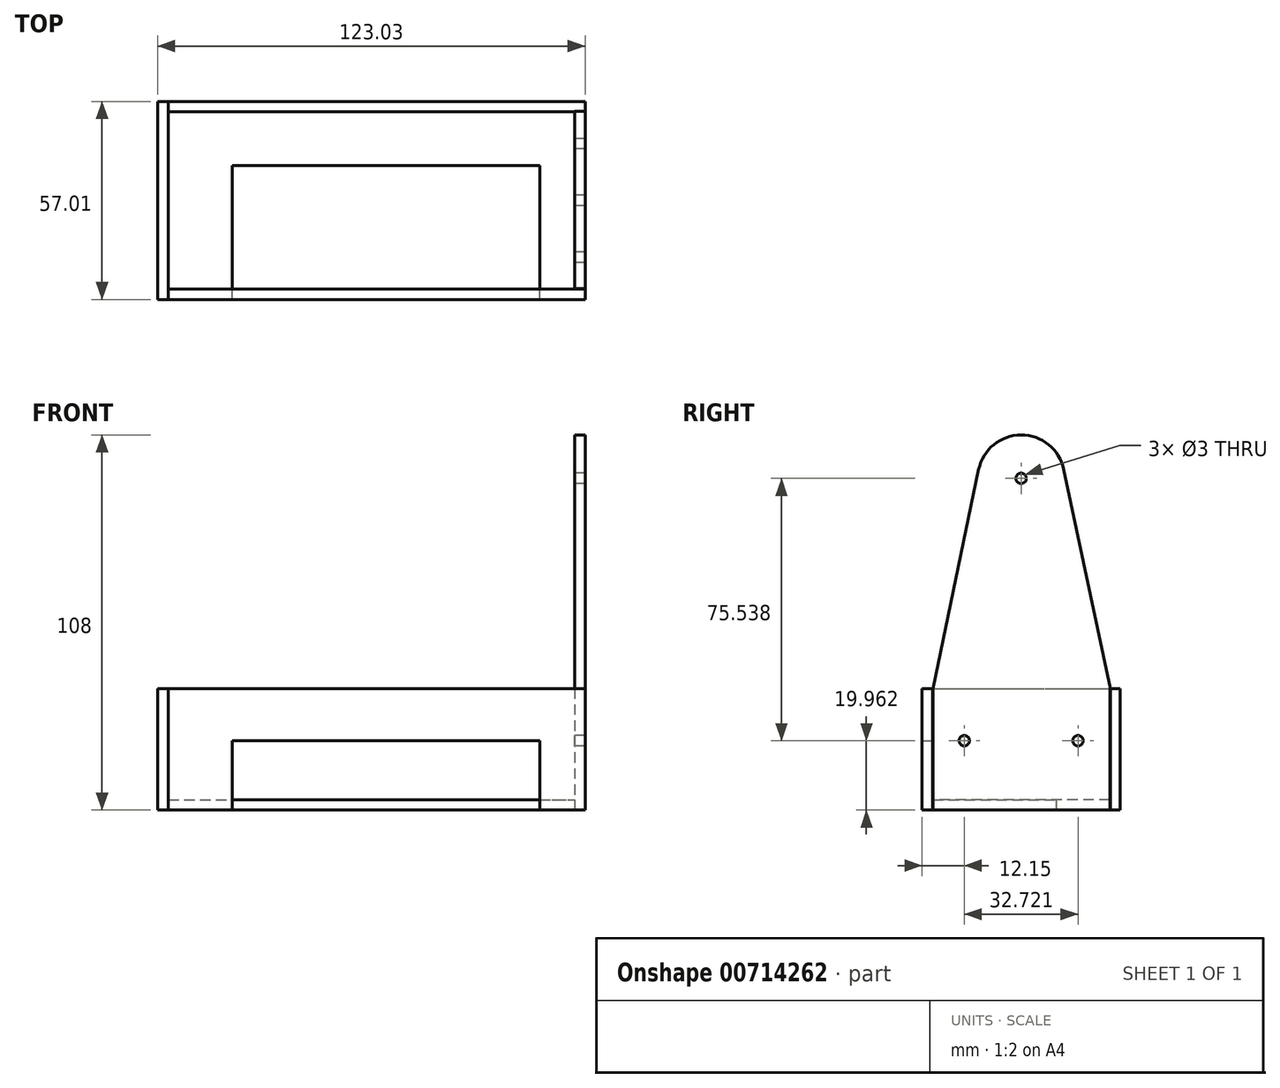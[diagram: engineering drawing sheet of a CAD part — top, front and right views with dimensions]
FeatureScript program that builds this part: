
annotation { "Feature Type Name" : "Feature", "Feature Type Description" : "" }
export const myFeature = defineFeature(function(context is Context, id is Id, definition is map)
    precondition{}
    {
        {
            var Q0;
            Q0=qCreatedBy(makeId("Top.planeOp"),FACE);
            var sketch = newSketch(context, id + "F0", { "sketchPlane" : qUnion([Q0])});
            skLineSegment(sketch, "E0.bottom", {"start": v(-58.5, 25.5) * mm, "end": v(58.5, 25.5) * mm});
            skLineSegment(sketch, "E0.top", {"start": v(-58.5, -25.5) * mm, "end": v(-40, -25.5) * mm});
            skLineSegment(sketch, "E0.left", {"start": v(-58.5, 25.5) * mm, "end": v(-58.5, -25.5) * mm});
            skLineSegment(sketch, "E0.right", {"start": v(58.5, 25.5) * mm, "end": v(58.5, -25.5) * mm});
            skPoint(sketch, "E0.middle", {"position": v(0, 0) * mm});
            skLineSegment(sketch, "E1", {"start": v(-40, -25.5) * mm, "end": v(-40, 10) * mm});
            skLineSegment(sketch, "E2", {"start": v(-40, 10) * mm, "end": v(48.5, 10) * mm});
            skLineSegment(sketch, "E3", {"start": v(48.5, 10) * mm, "end": v(48.5, -25.5) * mm});
            skLineSegment(sketch, "E4.trimOffspring", {"start": v(48.5, -25.5) * mm, "end": v(58.5, -25.5) * mm});
            skSolve(sketch);
        }
        {
            var Q0;
            Q0 = qSketchRegion(id + "F0", true);
            extrude(context, id + "F1", {"entities" : qUnion([Q0]), "depth" : 3 * mm, "offsetDistance" : 25 * mm});
        }
        {
            var Q0;
            Q0=makeQuery(id+"F1.opExtrude","SWEPT_FACE",FACE,{"disambiguationData":[OSD([sQuery(id+"F0.wireOp",EDGE,"E0.right")])]});
            cPlane(context, id + "F2", {"entities" : qUnion([Q0]), "cplaneType" : CPlaneType.OFFSET, "offset" : 0 * mm, "width" : 150 * mm, "height" : 150 * mm});
        }
        {
            var Q0;
            Q0=qCreatedBy(id+"F2.planeOp",FACE);
            var sketch = newSketch(context, id + "F3", { "sketchPlane" : qUnion([Q0])});
            skArc(sketch, "E5", {"start": v(12.23, 98.1) * mm, "mid": v(-0.02, 108) * mm, "end": v(-12.24, 98.05) * mm});
            skLineSegment(sketch, "E6", {"start": v(-25.38, 0) * mm, "end": v(25.62, 0) * mm});
            skLineSegment(sketch, "E7", {"start": v(-25.38, 35) * mm, "end": v(-25.38, 0) * mm});
            skLineSegment(sketch, "E8", {"start": v(25.62, 35) * mm, "end": v(25.62, 0) * mm});
            skLineSegment(sketch, "E9", {"start": v(-12.24, 98.05) * mm, "end": v(-25.38, 35) * mm});
            skLineSegment(sketch, "E10", {"start": v(12.23, 98.1) * mm, "end": v(25.62, 35) * mm});
            skCircle(sketch, "E11", {"center": v(-16.36, 19.96) * mm, "radius": 1.5 * mm});
            skCircle(sketch, "E12", {"center": v(0, 95.5) * mm, "radius": 1.5 * mm});
            skCircle(sketch, "E13.MirrorC", {"center": v(16.36, 19.96) * mm, "radius": 1.5 * mm});
            skSolve(sketch);
        }
        {
            var Q0;
            Q0 = qSketchRegion(id + "F3", true);
            extrude(context, id + "F4", {"entities" : qUnion([Q0]), "operationType" : NewBodyOperationType.ADD, "depth" : 3 * mm, "offsetDistance" : 25 * mm});
        }
        {
            var Q0;
            Q0=makeQuery(id+"F1.opExtrude","SWEPT_FACE",FACE,{"disambiguationData":[OSD([sQuery(id+"F0.wireOp",EDGE,"E0.top")])]});
            cPlane(context, id + "F5", {"entities" : qUnion([Q0]), "cplaneType" : CPlaneType.OFFSET, "offset" : 0 * mm, "width" : 150 * mm, "height" : 150 * mm});
        }
        {
            var Q0;
            Q0=qCreatedBy(id+"F5.planeOp",FACE);
            var sketch = newSketch(context, id + "F6", { "sketchPlane" : qUnion([Q0])});
            skLineSegment(sketch, "E14.bottom", {"start": v(-58.47, 35) * mm, "end": v(61.53, 35) * mm});
            skLineSegment(sketch, "E14.top", {"start": v(-58.47, 0) * mm, "end": v(-40, 0) * mm});
            skLineSegment(sketch, "E14.left", {"start": v(-58.47, 35) * mm, "end": v(-58.47, 0) * mm});
            skLineSegment(sketch, "E14.right", {"start": v(61.53, 35) * mm, "end": v(61.53, 0) * mm});
            skLineSegment(sketch, "E15", {"start": v(-40, 0) * mm, "end": v(-40, 20) * mm});
            skLineSegment(sketch, "E16", {"start": v(-40, 20) * mm, "end": v(48.5, 20) * mm});
            skLineSegment(sketch, "E17", {"start": v(48.5, 20) * mm, "end": v(48.5, 0) * mm});
            skLineSegment(sketch, "E18.trimOffspring", {"start": v(48.5, 0) * mm, "end": v(61.53, 0) * mm});
            skSolve(sketch);
        }
        {
            var Q0;
            Q0 = qSketchRegion(id + "F6", true);
            extrude(context, id + "F7", {"entities" : qUnion([Q0]), "operationType" : NewBodyOperationType.ADD, "depth" : 3 * mm, "offsetDistance" : 25 * mm});
        }
        {
            var Q0;
            Q0=makeQuery(id+"F1.opExtrude","SWEPT_FACE",FACE,{"disambiguationData":[OSD([sQuery(id+"F0.wireOp",EDGE,"E0.bottom")])]});
            cPlane(context, id + "F8", {"entities" : qUnion([Q0]), "cplaneType" : CPlaneType.OFFSET, "offset" : 0 * mm, "width" : 150 * mm, "height" : 150 * mm});
        }
        {
            var Q0;
            Q0=qCreatedBy(id+"F8.planeOp",FACE);
            var sketch = newSketch(context, id + "F9", { "sketchPlane" : qUnion([Q0])});
            skLineSegment(sketch, "E19.bottom", {"start": v(58.5, 0) * mm, "end": v(-61.5, 0) * mm});
            skLineSegment(sketch, "E19.top", {"start": v(58.5, 35) * mm, "end": v(-61.5, 35) * mm});
            skLineSegment(sketch, "E19.left", {"start": v(58.5, 0) * mm, "end": v(58.5, 35) * mm});
            skLineSegment(sketch, "E19.right", {"start": v(-61.5, 0) * mm, "end": v(-61.5, 35) * mm});
            skSolve(sketch);
        }
        {
            var Q0;
            Q0 = qSketchRegion(id + "F9", true);
            extrude(context, id + "F10", {"entities" : qUnion([Q0]), "depth" : 3 * mm, "offsetDistance" : 25 * mm});
        }
        {
            var Q0;
            Q0=makeQuery(id+"F1.opExtrude","SWEPT_FACE",FACE,{"disambiguationData":[OSD([sQuery(id+"F0.wireOp",EDGE,"E0.left")])]});
            cPlane(context, id + "F11", {"entities" : qUnion([Q0]), "cplaneType" : CPlaneType.OFFSET, "offset" : 0 * mm, "width" : 150 * mm, "height" : 150 * mm});
        }
        {
            var Q0;
            Q0=qCreatedBy(id+"F11.planeOp",FACE);
            var sketch = newSketch(context, id + "F12", { "sketchPlane" : qUnion([Q0])});
            skLineSegment(sketch, "E20.bottom", {"start": v(28.5, 0) * mm, "end": v(-28.5, 0) * mm});
            skLineSegment(sketch, "E20.top", {"start": v(28.5, 35) * mm, "end": v(-28.5, 35) * mm});
            skLineSegment(sketch, "E20.left", {"start": v(28.5, 0) * mm, "end": v(28.5, 35) * mm});
            skLineSegment(sketch, "E20.right", {"start": v(-28.5, 0) * mm, "end": v(-28.5, 35) * mm});
            skSolve(sketch);
        }
        {
            var Q0;
            Q0 = qSketchRegion(id + "F12", true);
            extrude(context, id + "F13", {"entities" : qUnion([Q0]), "operationType" : NewBodyOperationType.ADD, "depth" : 3 * mm, "offsetDistance" : 25 * mm});
        }
    });
